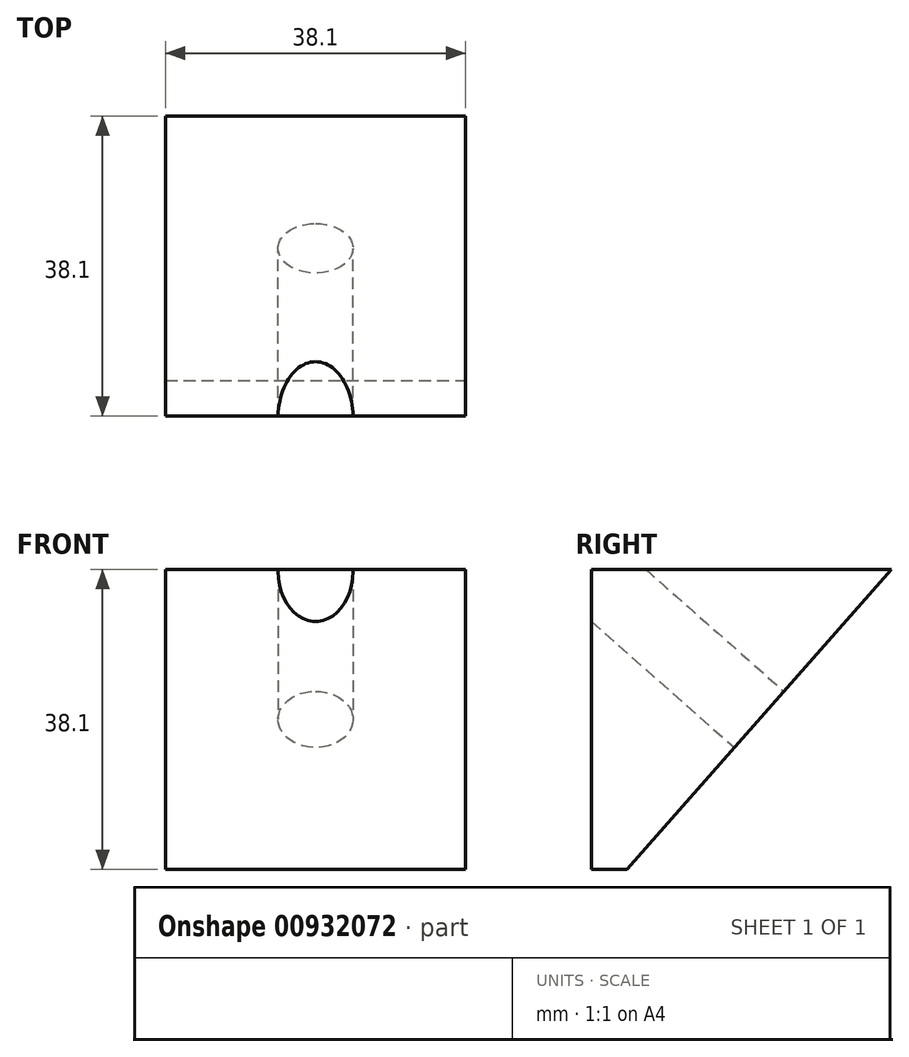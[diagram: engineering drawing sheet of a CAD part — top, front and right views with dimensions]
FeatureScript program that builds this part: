
annotation { "Feature Type Name" : "Feature", "Feature Type Description" : "" }
export const myFeature = defineFeature(function(context is Context, id is Id, definition is map)
    precondition{}
    {
        {
            var Q0;
            Q0=qCreatedBy(makeId("Front.planeOp"),FACE);
            var sketch = newSketch(context, id + "F0", { "sketchPlane" : qUnion([Q0])});
            skLineSegment(sketch, "E0", {"start": v(-19.05, 0) * mm, "end": v(0, 0) * mm});
            skLineSegment(sketch, "E1", {"start": v(0, 0) * mm, "end": v(19.05, 0) * mm});
            skLineSegment(sketch, "E2", {"start": v(-19.05, 0) * mm, "end": v(-19.05, 38.1) * mm});
            skLineSegment(sketch, "E3", {"start": v(-19.05, 38.1) * mm, "end": v(19.05, 38.1) * mm});
            skLineSegment(sketch, "E4", {"start": v(19.05, 38.1) * mm, "end": v(19.05, 0) * mm});
            skSolve(sketch);
        }
        {
            var Q0;
            Q0 = qSketchRegion(id + "F0", true);
            extrude(context, id + "F1", {"entities" : qUnion([Q0]), "depth" : 38.1 * mm, "offsetDistance" : 25.4 * mm});
        }
        {
            var Q0;
            Q0=qCreatedBy(makeId("Right.planeOp"),FACE);
            var sketch = newSketch(context, id + "F2", { "sketchPlane" : qUnion([Q0])});
            skLineSegment(sketch, "E5", {"start": v(0, 0) * mm, "end": v(0, 38.1) * mm});
            skLineSegment(sketch, "E6", {"start": v(0, 38.1) * mm, "end": v(-33.6, 0) * mm});
            skLineSegment(sketch, "E7", {"start": v(-33.6, 0) * mm, "end": v(0, 0) * mm});
            skSolve(sketch);
        }
        {
            var Q0;
            Q0 = qSketchRegion(id + "F2", true);
            extrude(context, id + "F3", {"entities" : qUnion([Q0]), "operationType" : NewBodyOperationType.REMOVE, "endBound" : BoundingType.THROUGH_ALL, "oppositeDirection" : true, "depth" : 25.4 * mm, "offsetDistance" : 25.4 * mm, "hasSecondDirection" : true, "secondDirectionBound" : SecondDirectionBoundingType.THROUGH_ALL, "secondDirectionOppositeDirection" : false, "secondDirectionDepth" : 25.4 * mm});
        }
        {
            var Q0;
            Q0=makeQuery(id+"F3.boolean.opBoolean","COPY",FACE,{"derivedFrom":makeQuery(id+"F3.opExtrude","SWEPT_FACE",FACE,{"disambiguationData":[OSD([sQuery(id+"F2.wireOp",EDGE,"E6")])]})});
            var sketch = newSketch(context, id + "F4", { "sketchPlane" : qUnion([Q0])});
            skCircle(sketch, "E8", {"center": v(0, 3.17) * mm, "radius": 4.76 * mm});
            skLineSegment(sketch, "E9", {"start": v(0, 28.57) * mm, "end": v(0, -22.23) * mm, "construction": true});
            skSolve(sketch);
        }
        {
            var Q0;
            Q0 = qSketchRegion(id + "F4", true);
            extrude(context, id + "F5", {"entities" : qUnion([Q0]), "operationType" : NewBodyOperationType.REMOVE, "endBound" : BoundingType.THROUGH_ALL, "oppositeDirection" : true, "depth" : 25.4 * mm, "offsetDistance" : 25.4 * mm});
        }
    });
